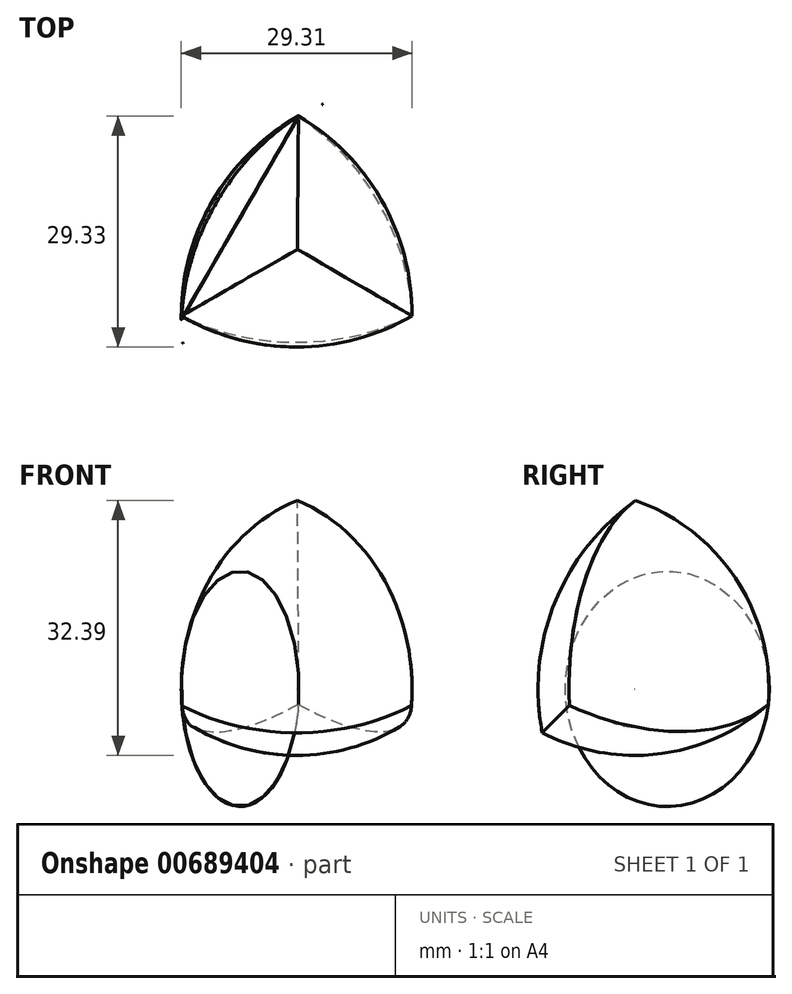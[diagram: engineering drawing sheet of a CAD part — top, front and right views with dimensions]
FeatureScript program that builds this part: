
annotation { "Feature Type Name" : "Feature", "Feature Type Description" : "" }
export const myFeature = defineFeature(function(context is Context, id is Id, definition is map)
    precondition{}
    {
        {
            var Q0;
            Q0=qCreatedBy(makeId("Top.planeOp"),FACE);
            var sketch = newSketch(context, id + "F0", { "sketchPlane" : qUnion([Q0])});
            skLineSegment(sketch, "E0", {"start": v(0, 16.93) * mm, "end": v(-14.66, -8.47) * mm});
            skLineSegment(sketch, "E1", {"start": v(14.66, -8.47) * mm, "end": v(0, 16.93) * mm});
            skLineSegment(sketch, "E2", {"start": v(14.66, -8.47) * mm, "end": v(-14.66, -8.47) * mm});
            skLineSegment(sketch, "E3", {"start": v(0, 0) * mm, "end": v(7.33, 4.23) * mm});
            skLineSegment(sketch, "E4", {"start": v(7.33, 4.23) * mm, "end": v(0, 0) * mm});
            skLineSegment(sketch, "E5", {"start": v(0, -8.47) * mm, "end": v(0, 0) * mm});
            skLineSegment(sketch, "E6", {"start": v(0, 0) * mm, "end": v(-7.33, 4.23) * mm});
            skLineSegment(sketch, "E7", {"start": v(-7.33, 4.23) * mm, "end": v(14.66, -8.47) * mm});
            skLineSegment(sketch, "E8", {"start": v(0, 16.93) * mm, "end": v(0, -8.47) * mm});
            skLineSegment(sketch, "E9", {"start": v(7.33, 4.23) * mm, "end": v(-14.66, -8.47) * mm});
            skSolve(sketch);
        }
        {
            var Q0;
            Q0=qCreatedBy(makeId("Top.planeOp"),FACE);
            var sketch = newSketch(context, id + "F1", { "sketchPlane" : qUnion([Q0])});
            skArc(sketch, "E10", {"start": v(14.64, -8.46) * mm, "mid": v(14.64, -8.45) * mm, "end": v(14.64, -8.44) * mm});
            skArc(sketch, "E11", {"start": v(-10.71, 6.18) * mm, "mid": v(-13.64, -0.88) * mm, "end": v(-14.63, -8.46) * mm});
            skLineSegment(sketch, "E12", {"start": v(0, 0) * mm, "end": v(-10.71, 6.18) * mm});
            skLineSegment(sketch, "E13", {"start": v(0, 0) * mm, "end": v(0, 0) * mm});
            skArc(sketch, "E14", {"start": v(-10.71, 6.18) * mm, "mid": v(0.02, -33.8) * mm, "end": v(40, -23.07) * mm});
            skLineSegment(sketch, "E15", {"start": v(-10.71, 6.18) * mm, "end": v(40, -23.07) * mm});
            skPoint(sketch, "E16.orphan", {"position": v(0, 16.9) * mm});
            skSolve(sketch);
        }
        {
            var Q0;
            Q0=qCreatedBy(makeId("Top.planeOp"),FACE);
            var sketch = newSketch(context, id + "F2", { "sketchPlane" : qUnion([Q0])});
            skPoint(sketch, "E17", {"position": v(0, -12.3) * mm});
            skPoint(sketch, "E18", {"position": v(10.67, 6.23) * mm});
            skArc(sketch, "E19", {"start": v(0, -12.3) * mm, "mid": v(29.28, 16.99) * mm, "end": v(0, 46.26) * mm, "construction": true});
            skArc(sketch, "E20", {"start": v(0, -12.3) * mm, "mid": v(29.28, 16.99) * mm, "end": v(0, 46.26) * mm});
            skLineSegment(sketch, "E21", {"start": v(0, 46.26) * mm, "end": v(0, -12.3) * mm});
            skSolve(sketch);
        }
        {
            var Q0;
            Q0=qCreatedBy(makeId("Top.planeOp"),FACE);
            var sketch = newSketch(context, id + "F3", { "sketchPlane" : qUnion([Q0])});
            skLineSegment(sketch, "E22", {"start": v(10.76, 6.44) * mm, "end": v(-40, -22.86) * mm});
            skArc(sketch, "E23", {"start": v(10.76, 6.44) * mm, "mid": v(-29.27, 17.17) * mm, "end": v(-40, -22.86) * mm});
            skSolve(sketch);
        }
        {
            var Q0;
            Q0=qCreatedBy(makeId("Front.planeOp"),FACE);
            var sketch = newSketch(context, id + "F4", { "sketchPlane" : qUnion([Q0])});
            skLineSegment(sketch, "E24", {"start": v(0, 0) * mm, "end": v(0, 16.94) * mm});
            skLineSegment(sketch, "E25", {"start": v(0, 16.94) * mm, "end": v(0, -8.46) * mm});
            skArc(sketch, "E26", {"start": v(0, -8.46) * mm, "mid": v(25.4, 16.94) * mm, "end": v(0, 42.34) * mm});
            skLineSegment(sketch, "E27", {"start": v(0, 42.34) * mm, "end": v(0, -8.46) * mm});
            skSolve(sketch);
        }
        {
            var Q0;
            {var subQ0=sQuery(id+"F4.wireOp",EDGE,"E26");Q0=makeQuery(id+"F4.imprint","IMPRINT",FACE,{"disambiguationData":[TD([[makeQuery(id+"F4.imprint","IMPRINT",EDGE,{"derivedFrom":subQ0}),1.0]])]});}
            var Q1;
            Q1=sQuery(id+"F4.wireOp",EDGE,"E27");
            revolve(context, id + "F5", {"entities" : qUnion([Q0]), "axis" : qUnion([Q1]), "revolveType" : RevolveType.FULL});
        }
        {
            var Q0;
            Q0=makeQuery(id+"F2.imprint","IMPRINT",FACE,{"disambiguationData":[TD([[makeQuery(id+"F2.imprint","IMPRINT",EDGE,{"derivedFrom":sQuery(id+"F2.wireOp",EDGE,"E20")}),1.0]])]});
            var Q1;
            Q1=sQuery(id+"F2.wireOp",EDGE,"E21");
            revolve(context, id + "F6", {"operationType" : NewBodyOperationType.INTERSECT, "entities" : qUnion([Q0]), "axis" : qUnion([Q1]), "revolveType" : RevolveType.FULL, "surfaceOperationType" : NewSurfaceOperationType.NEW});
        }
        {
            var Q0;
            Q0=qCreatedBy(makeId("Top.planeOp"),FACE);
            var sketch = newSketch(context, id + "F7", { "sketchPlane" : qUnion([Q0])});
            skSolve(sketch);
        }
        {
            var Q0;
            Q0 = qSketchRegion(id + "F7", true);
            var Q1;
            Q1=makeQuery(id+"F3.imprint","IMPRINT",FACE,{"disambiguationData":[TD([[makeQuery(id+"F3.imprint","IMPRINT",EDGE,{"derivedFrom":sQuery(id+"F3.wireOp",EDGE,"E22")}),-1.0]])]});
            var Q2;
            Q2=sQuery(id+"F3.wireOp",EDGE,"E22");
            revolve(context, id + "F8", {"operationType" : NewBodyOperationType.INTERSECT, "entities" : qUnion([Q0, Q1]), "axis" : qUnion([Q2]), "revolveType" : RevolveType.FULL, "surfaceOperationType" : NewSurfaceOperationType.NEW});
        }
        {
            var Q0;
            Q0=makeQuery(id+"F1.imprint","IMPRINT",FACE,{"disambiguationData":[TD([[makeQuery(id+"F1.imprint","IMPRINT",EDGE,{"derivedFrom":sQuery(id+"F1.wireOp",EDGE,"E12")}),1.0]])]});
            var Q1;
            Q1=sQuery(id+"F1.wireOp",EDGE,"E15");
            revolve(context, id + "F9", {"operationType" : NewBodyOperationType.INTERSECT, "entities" : qUnion([Q0]), "axis" : qUnion([Q1]), "revolveType" : RevolveType.FULL, "surfaceOperationType" : NewSurfaceOperationType.NEW});
        }
    });
